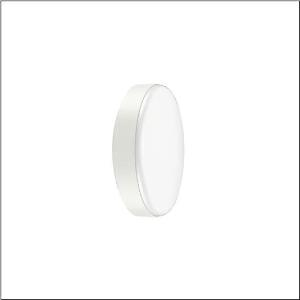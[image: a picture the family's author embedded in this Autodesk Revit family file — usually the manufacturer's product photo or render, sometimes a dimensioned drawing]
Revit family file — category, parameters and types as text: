
# Revit family: rondel_31_51wc10da32a
name_source: partatom
category: Lighting Fixtures
units: mm (PartAtom-declared; Revit-internal decimal feet)

## family parameters
Cut with Voids When Loaded = No
Host = Face
Light Source = No
Part Type = Normal
Room Calculation Point = No
Round Connector Dimension = Use Diameter
Shared = No

## types (1)
- Rondel 31 (1 x LED, 2450 lm, 19 W, 3000K)
    Apparent Load = 19 VA
    CIE Flux Codes = 44 75 94 94 100
    Color Rendering = 80
    Color Temperature = 3000K
    Default Elevation = 1800 mm
    Description = Rondel 31, wall and ceiling luminaire, primary optical cover: cover, of PC, opal, light emission: direct distribution, primary light characteristic: symmetric, installation type: surface-mounted, LED, rated luminous flux: 2.450lm, luminous efficacy: 129lm/W, light colour: 830, colour temperature: 3000K, with terminal, 5-pole, max. 2.5mm², mains connection: 220..240V, AC, 50/60Hz, rated input power: 19W, luminaire housing, of PC, traffic white (RAL 9016), diameter: 350mm, protection rating (complete): IP65, insulation class (complete): insulation class II (safety insulation), certification: CE, impact resistance: IK10, permissible operating ambient temperature: -20..+40°C, permissible storage temperature: -20..+60°C, packaging unit: 1 piece
    Height = 97 mm
    Lamp = 1 x LED
    Lamp Light Flux = 2450 lm
    Lamp Power = 19 W
    Lamp count = 1
    Length = 350 mm
    Luminous efficacy = 129 lm/W
    Manufacturer = Siteco
    ModVariant = No
    Model = 51WC10DA32A
    Mounting Place = Ceiling
    Mounting Type = Surface mounted
    Number of Poles = 1
    OnlyDefault = Yes
    Power Factor = 1
    Product Name = Rondel 31
    Product group = wall and ceiling luminaire
    ProductGroupID = 301
    Protection Class = Protection class II
    Protection Degree = IP 65
    RLX_Detail_Level = 1
    RLX_Emergency_Light_Flux = 0 lm
    RLX_Emergency_Type = 0
    RLX_Emergency_Type_DB = No
    RlxData = <blob elided: 29573 chars, md5=312fea2e>
    Socket = socket
    Standby Power = 0 W
    System Light Flux = 2450 lm
    System Power = 19 W
    Type Comments = Product without accessories
    Type Image = l_1007027.jpg
    URL = http://relux.com
    VarID = ---
    Voltage = 0 V
    Weight = 0.00 kg
    Width = 0 mm  [stored 0 ft]

note: [stored X ft] marks values corroborated as IEEE doubles in the binary element streams (Revit-internal decimal feet)

## geometry (parser evidence)
native form markers: Blend x4, Sweep x11
no freeform markers — native parametric forms only
